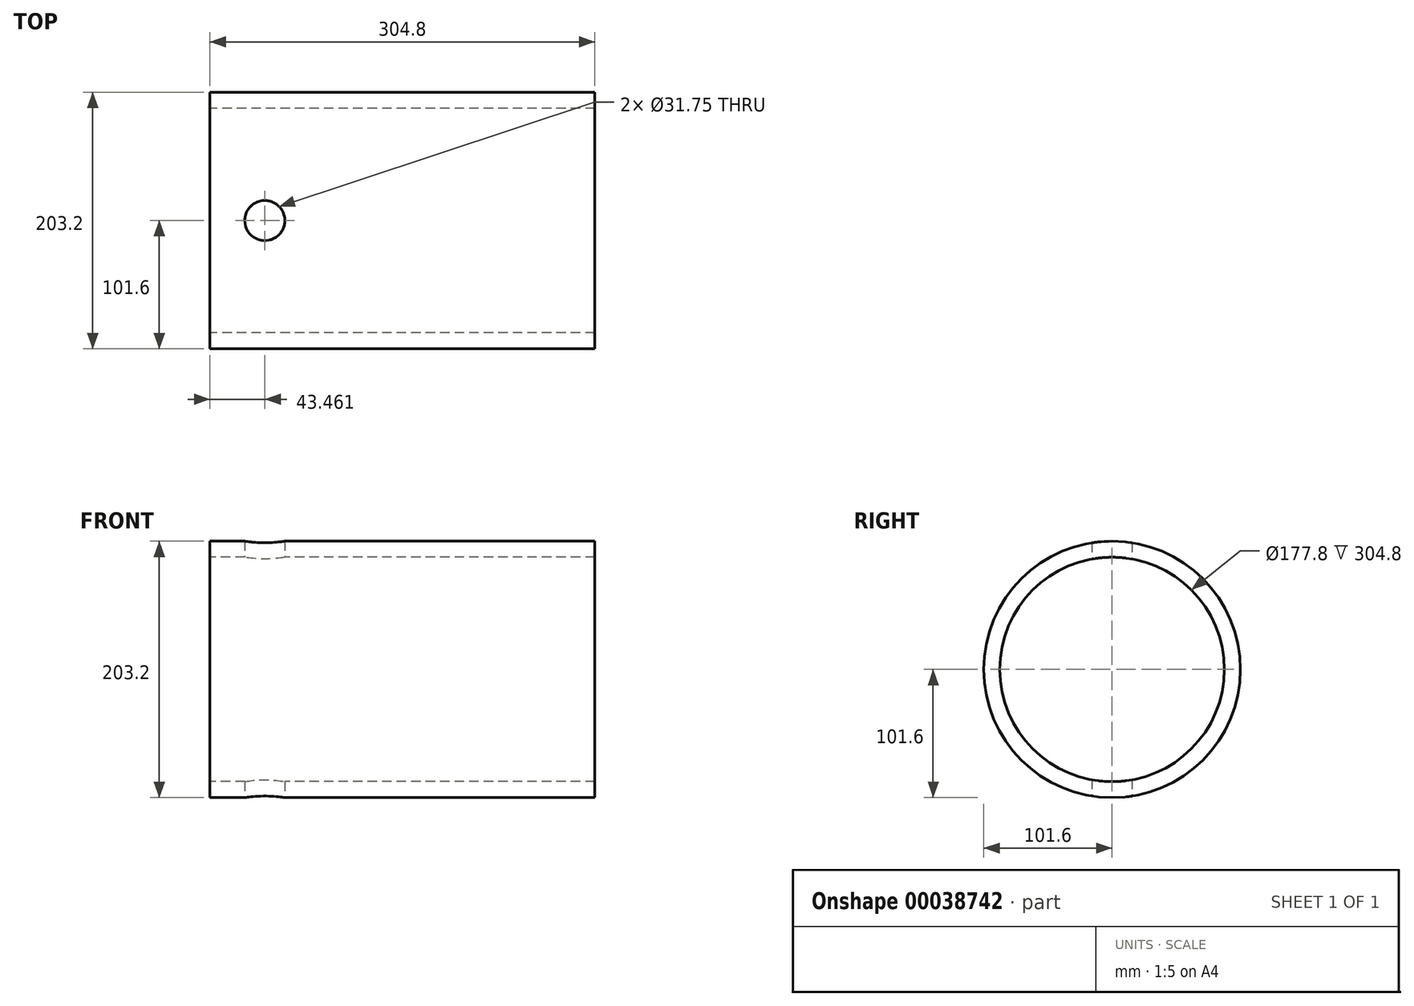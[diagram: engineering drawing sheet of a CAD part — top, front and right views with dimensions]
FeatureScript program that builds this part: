
annotation { "Feature Type Name" : "Feature", "Feature Type Description" : "" }
export const myFeature = defineFeature(function(context is Context, id is Id, definition is map)
    precondition{}
    {
        {
            var Q0;
            Q0=qCreatedBy(makeId("Front.planeOp"),FACE);
            var sketch = newSketch(context, id + "F0", { "sketchPlane" : qUnion([Q0])});
            skLineSegment(sketch, "E0", {"start": v(0, 101.6) * mm, "end": v(304.8, 101.6) * mm});
            skLineSegment(sketch, "E1", {"start": v(0, 101.6) * mm, "end": v(0, 88.9) * mm});
            skLineSegment(sketch, "E2", {"start": v(0, 88.9) * mm, "end": v(304.8, 88.9) * mm});
            skLineSegment(sketch, "E3", {"start": v(304.8, 101.6) * mm, "end": v(304.8, 88.9) * mm});
            skSolve(sketch);
        }
        {
            var Q0;
            Q0=qCreatedBy(makeId("Front.planeOp"),FACE);
            var sketch = newSketch(context, id + "F1", { "sketchPlane" : qUnion([Q0])});
            skLineSegment(sketch, "E4", {"start": v(0, 0) * mm, "end": v(113.14, 0) * mm});
            skSolve(sketch);
        }
        {
            var Q0;
            Q0 = qSketchRegion(id + "F0", true);
            var Q1;
            Q1=sQuery(id+"F1.wireOp",EDGE,"E4");
            revolve(context, id + "F2", {"entities" : qUnion([Q0]), "axis" : qUnion([Q1]), "revolveType" : RevolveType.FULL});
        }
        {
            var Q0;
            Q0=qCreatedBy(makeId("Top.planeOp"),FACE);
            var sketch = newSketch(context, id + "F3", { "sketchPlane" : qUnion([Q0])});
            skCircle(sketch, "E5", {"center": v(43.46, 0) * mm, "radius": 15.88 * mm});
            skSolve(sketch);
        }
        {
            var Q0;
            Q0 = qSketchRegion(id + "F3", true);
            extrude(context, id + "F4", {"entities" : qUnion([Q0]), "operationType" : NewBodyOperationType.REMOVE, "endBound" : BoundingType.THROUGH_ALL, "depth" : 25.4 * mm, "hasSecondDirection" : true, "secondDirectionBound" : SecondDirectionBoundingType.THROUGH_ALL, "secondDirectionOppositeDirection" : true, "secondDirectionDepth" : 25.4 * mm});
        }
    });
